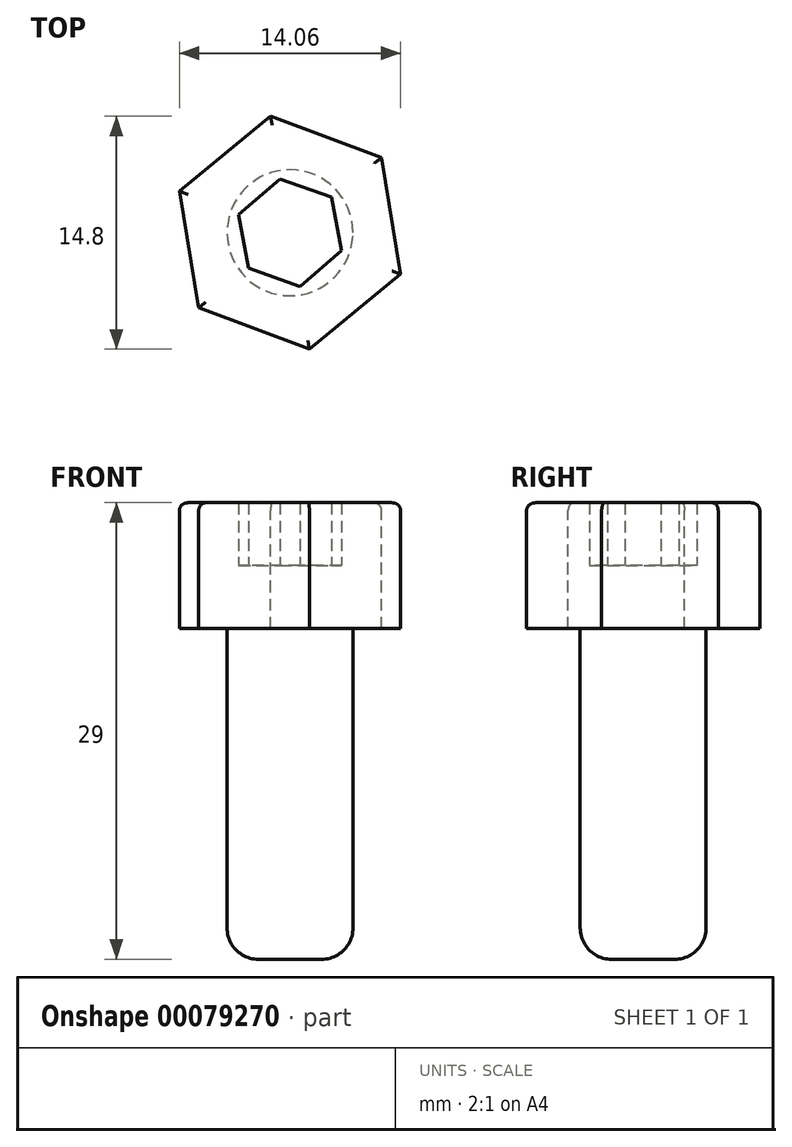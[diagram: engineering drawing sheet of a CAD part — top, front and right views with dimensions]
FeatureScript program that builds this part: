
annotation { "Feature Type Name" : "Feature", "Feature Type Description" : "" }
export const myFeature = defineFeature(function(context is Context, id is Id, definition is map)
    precondition{}
    {
        {
            var Q0;
            Q0=qCreatedBy(makeId("Top.planeOp"),FACE);
            var sketch = newSketch(context, id + "F0", { "sketchPlane" : qUnion([Q0])});
            skCircle(sketch, "E0", {"center": v(0, 0) * mm, "radius": 4 * mm});
            skCircle(sketch, "E1.cCircle", {"center": v(0, 0) * mm, "radius": 3 * mm, "construction": true});
            skLineSegment(sketch, "E1.0", {"start": v(-3.27, 1.15) * mm, "end": v(-0.64, 3.4) * mm});
            skLineSegment(sketch, "E1.1", {"start": v(-0.64, 3.4) * mm, "end": v(2.63, 2.26) * mm});
            skLineSegment(sketch, "E1.2", {"start": v(2.63, 2.26) * mm, "end": v(3.27, -1.15) * mm});
            skLineSegment(sketch, "E1.3", {"start": v(3.27, -1.15) * mm, "end": v(0.64, -3.4) * mm});
            skLineSegment(sketch, "E1.4", {"start": v(0.64, -3.4) * mm, "end": v(-2.63, -2.26) * mm});
            skLineSegment(sketch, "E1.5", {"start": v(-2.63, -2.26) * mm, "end": v(-3.27, 1.15) * mm});
            skPoint(sketch, "E1.0.midPoint", {"position": v(-1.96, 2.28) * mm});
            skCircle(sketch, "E2", {"center": v(0, 0) * mm, "radius": 6.5 * mm});
            skCircle(sketch, "E3.cCircle", {"center": v(0, 0) * mm, "radius": 6.5 * mm, "construction": true});
            skLineSegment(sketch, "E3.0", {"start": v(-7.03, 2.64) * mm, "end": v(-1.23, 7.4) * mm});
            skLineSegment(sketch, "E3.1", {"start": v(-1.23, 7.4) * mm, "end": v(5.8, 4.77) * mm});
            skLineSegment(sketch, "E3.2", {"start": v(5.8, 4.77) * mm, "end": v(7.03, -2.64) * mm});
            skLineSegment(sketch, "E3.3", {"start": v(7.03, -2.64) * mm, "end": v(1.23, -7.4) * mm});
            skLineSegment(sketch, "E3.4", {"start": v(1.23, -7.4) * mm, "end": v(-5.8, -4.77) * mm});
            skLineSegment(sketch, "E3.5", {"start": v(-5.8, -4.77) * mm, "end": v(-7.03, 2.64) * mm});
            skPoint(sketch, "E3.0.midPoint", {"position": v(-4.13, 5.02) * mm});
            skSolve(sketch);
        }
        {
            var Q0;
            Q0=qSketchRegion(id+"F0",true);
            var Q1;
            Q1=makeQuery(id+"F0.imprint","IMPRINT",FACE,{"disambiguationData":[TD([[makeQuery(id+"F0.imprint","IMPRINT",EDGE,{"derivedFrom":sQuery(id+"F0.wireOp",EDGE,"E0")}),1.0]])]});
            var Q2;
            Q2=makeQuery(id+"F0.imprint","IMPRINT",FACE,{"disambiguationData":[TD([[makeQuery(id+"F0.imprint","IMPRINT",EDGE,{"derivedFrom":sQuery(id+"F0.wireOp",EDGE,"E1.0")}),-1.0]])]});
            extrude(context, id + "F1", {"entities" : qUnion([Q0, Q1, Q2]), "oppositeDirection" : true, "depth" : 4 * mm});
        }
        {
            var Q0;
            Q0=makeQuery(id+"F0.imprint","IMPRINT",FACE,{"disambiguationData":[TD([[makeQuery(id+"F0.imprint","IMPRINT",EDGE,{"derivedFrom":sQuery(id+"F0.wireOp",EDGE,"E0")}),1.0]])]});
            var Q1;
            {var subQ0=sQuery(id+"F0.wireOp",EDGE,"E3.1");var subQ1=sQuery(id+"F0.wireOp",EDGE,"E2");var subQ2=makeQuery(id+"F0.imprint","INTERSECT",VERTEX,{"derivedFrom":[subQ1,subQ0]});Q1=makeQuery(id+"F0.imprint","IMPRINT",FACE,{"disambiguationData":[TD([[makeQuery(id+"F0.imprint","IMPRINT",EDGE,{"disambiguationData":[TD([[subQ2,-1.0]])],"derivedFrom":subQ1}),-1.0]])]});}
            var Q2;
            {var subQ0=sQuery(id+"F0.wireOp",EDGE,"E3.0");var subQ1=sQuery(id+"F0.wireOp",EDGE,"E2");var subQ2=makeQuery(id+"F0.imprint","INTERSECT",VERTEX,{"derivedFrom":[subQ1,subQ0]});Q2=makeQuery(id+"F0.imprint","IMPRINT",FACE,{"disambiguationData":[TD([[makeQuery(id+"F0.imprint","IMPRINT",EDGE,{"disambiguationData":[TD([[subQ2,-1.0]])],"derivedFrom":subQ1}),-1.0]])]});}
            var Q3;
            {var subQ0=sQuery(id+"F0.wireOp",EDGE,"E3.5");var subQ1=sQuery(id+"F0.wireOp",EDGE,"E2");var subQ2=makeQuery(id+"F0.imprint","INTERSECT",VERTEX,{"derivedFrom":[subQ1,subQ0]});Q3=makeQuery(id+"F0.imprint","IMPRINT",FACE,{"disambiguationData":[TD([[makeQuery(id+"F0.imprint","IMPRINT",EDGE,{"disambiguationData":[TD([[subQ2,-1.0]])],"derivedFrom":subQ1}),-1.0]])]});}
            var Q4;
            {var subQ0=sQuery(id+"F0.wireOp",EDGE,"E3.1");var subQ1=sQuery(id+"F0.wireOp",EDGE,"E2");var subQ2=makeQuery(id+"F0.imprint","INTERSECT",VERTEX,{"derivedFrom":[subQ1,subQ0]});Q4=makeQuery(id+"F0.imprint","IMPRINT",FACE,{"disambiguationData":[TD([[makeQuery(id+"F0.imprint","IMPRINT",EDGE,{"disambiguationData":[TD([[subQ2,1.0]])],"derivedFrom":subQ1}),-1.0]])]});}
            var Q5;
            {var subQ0=sQuery(id+"F0.wireOp",EDGE,"E3.2");var subQ1=sQuery(id+"F0.wireOp",EDGE,"E2");var subQ2=makeQuery(id+"F0.imprint","INTERSECT",VERTEX,{"derivedFrom":[subQ1,subQ0]});Q5=makeQuery(id+"F0.imprint","IMPRINT",FACE,{"disambiguationData":[TD([[makeQuery(id+"F0.imprint","IMPRINT",EDGE,{"disambiguationData":[TD([[subQ2,1.0]])],"derivedFrom":subQ1}),-1.0]])]});}
            var Q6;
            {var subQ0=sQuery(id+"F0.wireOp",EDGE,"E3.4");var subQ1=sQuery(id+"F0.wireOp",EDGE,"E2");var subQ2=makeQuery(id+"F0.imprint","INTERSECT",VERTEX,{"derivedFrom":[subQ1,subQ0]});Q6=makeQuery(id+"F0.imprint","IMPRINT",FACE,{"disambiguationData":[TD([[makeQuery(id+"F0.imprint","IMPRINT",EDGE,{"disambiguationData":[TD([[subQ2,-1.0]])],"derivedFrom":subQ1}),-1.0]])]});}
            var Q7;
            Q7=makeQuery(id+"F0.imprint","IMPRINT",FACE,{"disambiguationData":[TD([[makeQuery(id+"F0.imprint","IMPRINT",EDGE,{"derivedFrom":sQuery(id+"F0.wireOp",EDGE,"E0")}),-1.0]])]});
            extrude(context, id + "F2", {"entities" : qUnion([Q0, Q1, Q2, Q3, Q4, Q5, Q6, Q7]), "operationType" : NewBodyOperationType.ADD, "depth" : 4 * mm});
        }
        {
            var Q0;
            Q0=makeQuery(id+"F0.imprint","IMPRINT",FACE,{"disambiguationData":[TD([[makeQuery(id+"F0.imprint","IMPRINT",EDGE,{"derivedFrom":sQuery(id+"F0.wireOp",EDGE,"E1.0")}),-1.0]])]});
            var Q1;
            Q1=makeQuery(id+"F0.imprint","IMPRINT",FACE,{"disambiguationData":[TD([[makeQuery(id+"F0.imprint","IMPRINT",EDGE,{"derivedFrom":sQuery(id+"F0.wireOp",EDGE,"E0")}),1.0]])]});
            extrude(context, id + "F3", {"entities" : qUnion([Q0, Q1]), "operationType" : NewBodyOperationType.ADD, "oppositeDirection" : true, "depth" : 25 * mm});
        }
        {
            var Q0;
            Q0=makeQuery(id+"F3.opExtrude","CAP_EDGE",EDGE,{"disambiguationData":[OSD([sQuery(id+"F0.wireOp",EDGE,"E0")])],"isStart":false});
            fillet(context, id + "F4", {"entities" : qUnion([Q0]), "radius" : 2 * mm, "tangentPropagation" : true, "allowEdgeOverflow" : false});
        }
        {
            var Q0;
            Q0=makeQuery(id+"F2.opExtrude","CAP_EDGE",EDGE,{"disambiguationData":[OSD([sQuery(id+"F0.wireOp",EDGE,"E3.5")])],"isStart":false});
            var Q1;
            Q1=makeQuery(id+"F2.opExtrude","CAP_EDGE",EDGE,{"disambiguationData":[OSD([sQuery(id+"F0.wireOp",EDGE,"E3.4")])],"isStart":false});
            var Q2;
            Q2=makeQuery(id+"F2.opExtrude","CAP_EDGE",EDGE,{"disambiguationData":[OSD([sQuery(id+"F0.wireOp",EDGE,"E3.3")])],"isStart":false});
            var Q3;
            Q3=makeQuery(id+"F2.opExtrude","CAP_EDGE",EDGE,{"disambiguationData":[OSD([sQuery(id+"F0.wireOp",EDGE,"E3.2")])],"isStart":false});
            var Q4;
            Q4=makeQuery(id+"F2.opExtrude","CAP_EDGE",EDGE,{"disambiguationData":[OSD([sQuery(id+"F0.wireOp",EDGE,"E3.1")])],"isStart":false});
            var Q5;
            Q5=makeQuery(id+"F2.opExtrude","CAP_EDGE",EDGE,{"disambiguationData":[OSD([sQuery(id+"F0.wireOp",EDGE,"E3.0")])],"isStart":false});
            fillet(context, id + "F5", {"entities" : qUnion([Q0, Q1, Q2, Q3, Q4, Q5]), "radius" : 0.5 * mm, "tangentPropagation" : true, "allowEdgeOverflow" : false});
        }
    });
